# Revit family: Shower-Digital_Interface-KOHLER-DTV_Mode-K-29202
name_source: partatom
category: Specialty Equipment
revit_build: Autodesk Revit 2017 (Build: 20160225_1515(x64)
units: mm (PartAtom-declared; Revit-internal decimal feet)

## family parameters
Cut with Voids When Loaded = No
Host = Face
OmniClass Number = 23.31.25.00
Part Type = Normal
Room Calculation Point = No
Round Connector Dimension = Use Diameter
Shared = No

## types (4) — shared parameters
ADA Compliant = No
Assembly Code = C1030200
Date Modified = 07/02/2020
Default Elevation = 42"
Height = 2 1/2"
Length = 1 9/16"
Manufacturer = KOHLER Co.
Master Format 2014 = 10 28 00
Master Format 2014 Name = Toilet, Bath, and Laundry Accessories
Material = Premium Metal Construction
Product Documentation Link = https://www.us.kohler.com
Product Name = DTV Mode
Product Page URL = http://www.us.kohler.com
URL = https://www.us.kohler.com
WaterSense Certified = No
Width = 2 1/2"

## per-type parameters (varying)
| type | Description | Finish | Model | Type |
| Dual Outlet,CP-Polished Chrome | Dual-outlet shower digital interface | Kohler-Metal-CP-Polished_Chrome | K-29202-CP | 1 |
| Dual Outlet,BL-Matte Black | Dual-outlet shower digital interface | Kohler-Metal-BL-Matte_Black | K-29202-BL | 2 |
| Dual Outlet With Eco Mode Diverter,CP-Polished Chrome | Dual-outlet shower digital interface with eco-mode diverter | Kohler-Metal-CP-Polished_Chrome | K-29202-E-CP | 3 |
| Dual Outlet With Eco Mode Diverter,BL-Matte Black | Dual-outlet shower digital interface with eco-mode diverter | Kohler-Metal-BL-Matte_Black | K-29202-E-BL | 4 |

## geometry (parser evidence)
native form markers: Sweep x6
no freeform markers — native parametric forms only
